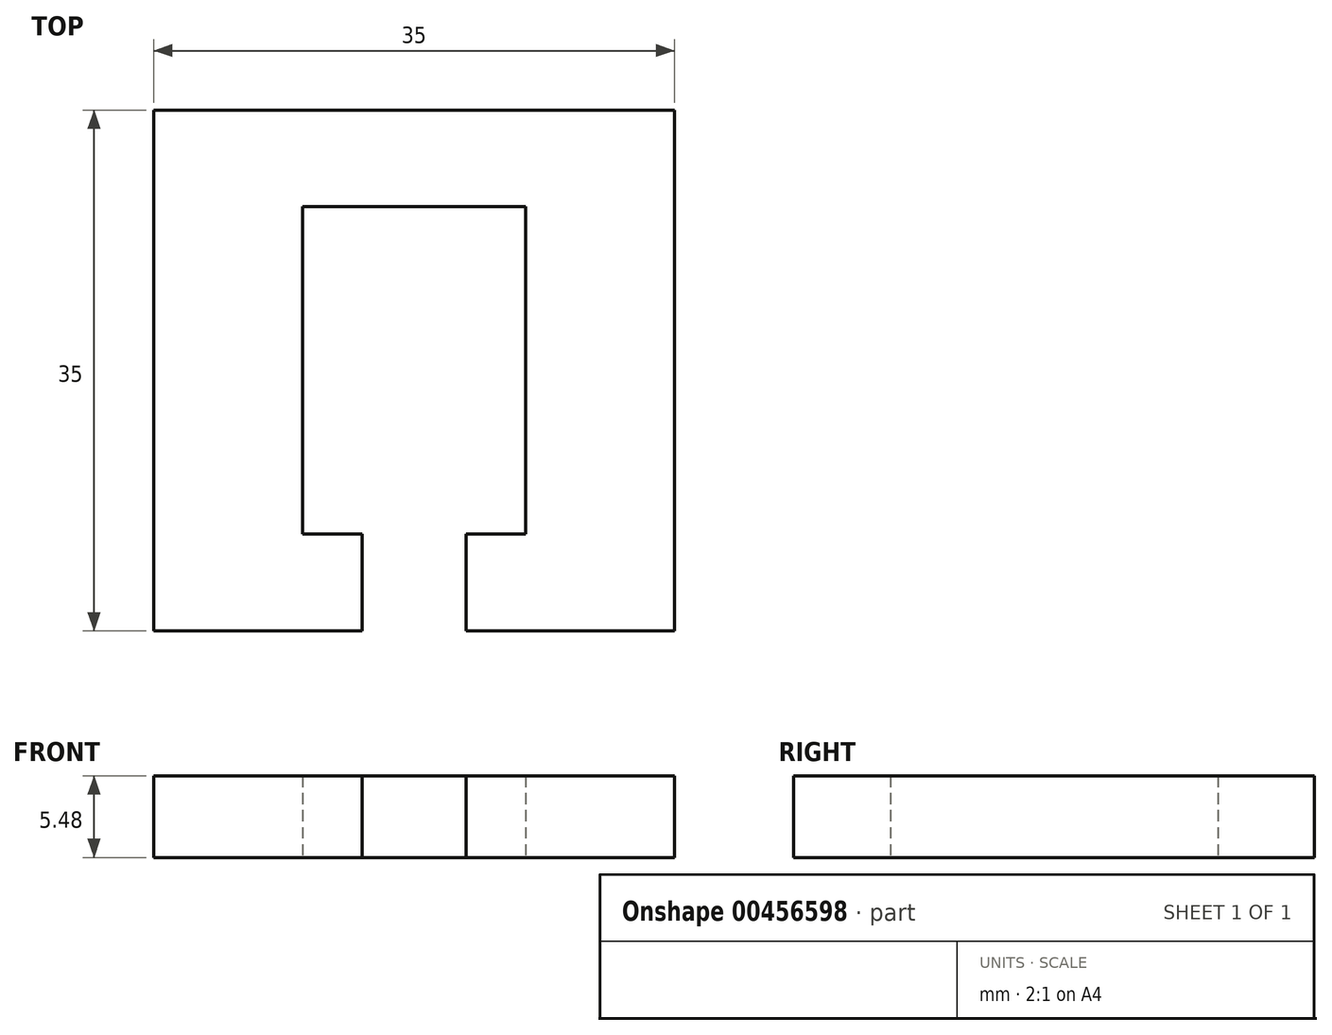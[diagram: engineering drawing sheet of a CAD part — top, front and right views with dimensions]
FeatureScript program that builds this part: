
annotation { "Feature Type Name" : "Feature", "Feature Type Description" : "" }
export const myFeature = defineFeature(function(context is Context, id is Id, definition is map)
    precondition{}
    {
        {
            var Q0;
            Q0=qCreatedBy(makeId("Top.planeOp"),FACE);
            var sketch = newSketch(context, id + "F0", { "sketchPlane" : qUnion([Q0])});
            skLineSegment(sketch, "E0.bottom", {"start": v(17.5, 17.5) * mm, "end": v(-17.5, 17.5) * mm});
            skLineSegment(sketch, "E0.top", {"start": v(17.5, -17.5) * mm, "end": v(3.5, -17.5) * mm});
            skLineSegment(sketch, "E0.left", {"start": v(17.5, 17.5) * mm, "end": v(17.5, -17.5) * mm});
            skLineSegment(sketch, "E0.right", {"start": v(-17.5, 17.5) * mm, "end": v(-17.5, -17.5) * mm});
            skPoint(sketch, "E0.middle", {"position": v(0, 0) * mm});
            skLineSegment(sketch, "E1.bottom", {"start": v(7.5, 11) * mm, "end": v(-7.5, 11) * mm});
            skLineSegment(sketch, "E1.top", {"start": v(7.5, -11) * mm, "end": v(3.5, -11) * mm});
            skLineSegment(sketch, "E1.left", {"start": v(7.5, 11) * mm, "end": v(7.5, -11) * mm});
            skLineSegment(sketch, "E1.right", {"start": v(-7.5, 11) * mm, "end": v(-7.5, -11) * mm});
            skLineSegment(sketch, "E2.left", {"start": v(3.5, -17.5) * mm, "end": v(3.5, -11) * mm});
            skLineSegment(sketch, "E2.right", {"start": v(-3.5, -17.5) * mm, "end": v(-3.5, -11) * mm});
            skPoint(sketch, "E2.middle", {"position": v(0, -11) * mm});
            skPoint(sketch, "E3.orphan", {"position": v(-3.5, -4.5) * mm});
            skPoint(sketch, "E4.orphan", {"position": v(3.5, -4.5) * mm});
            skLineSegment(sketch, "E5.trimOffspring", {"start": v(-3.5, -11) * mm, "end": v(-7.5, -11) * mm});
            skLineSegment(sketch, "E6.trimOffspring", {"start": v(-3.5, -17.5) * mm, "end": v(-17.5, -17.5) * mm});
            skSolve(sketch);
        }
        {
            var Q0;
            Q0 = qSketchRegion(id + "F0", true);
            extrude(context, id + "F1", {"entities" : qUnion([Q0]), "depth" : 5.48 * mm});
        }
    });
